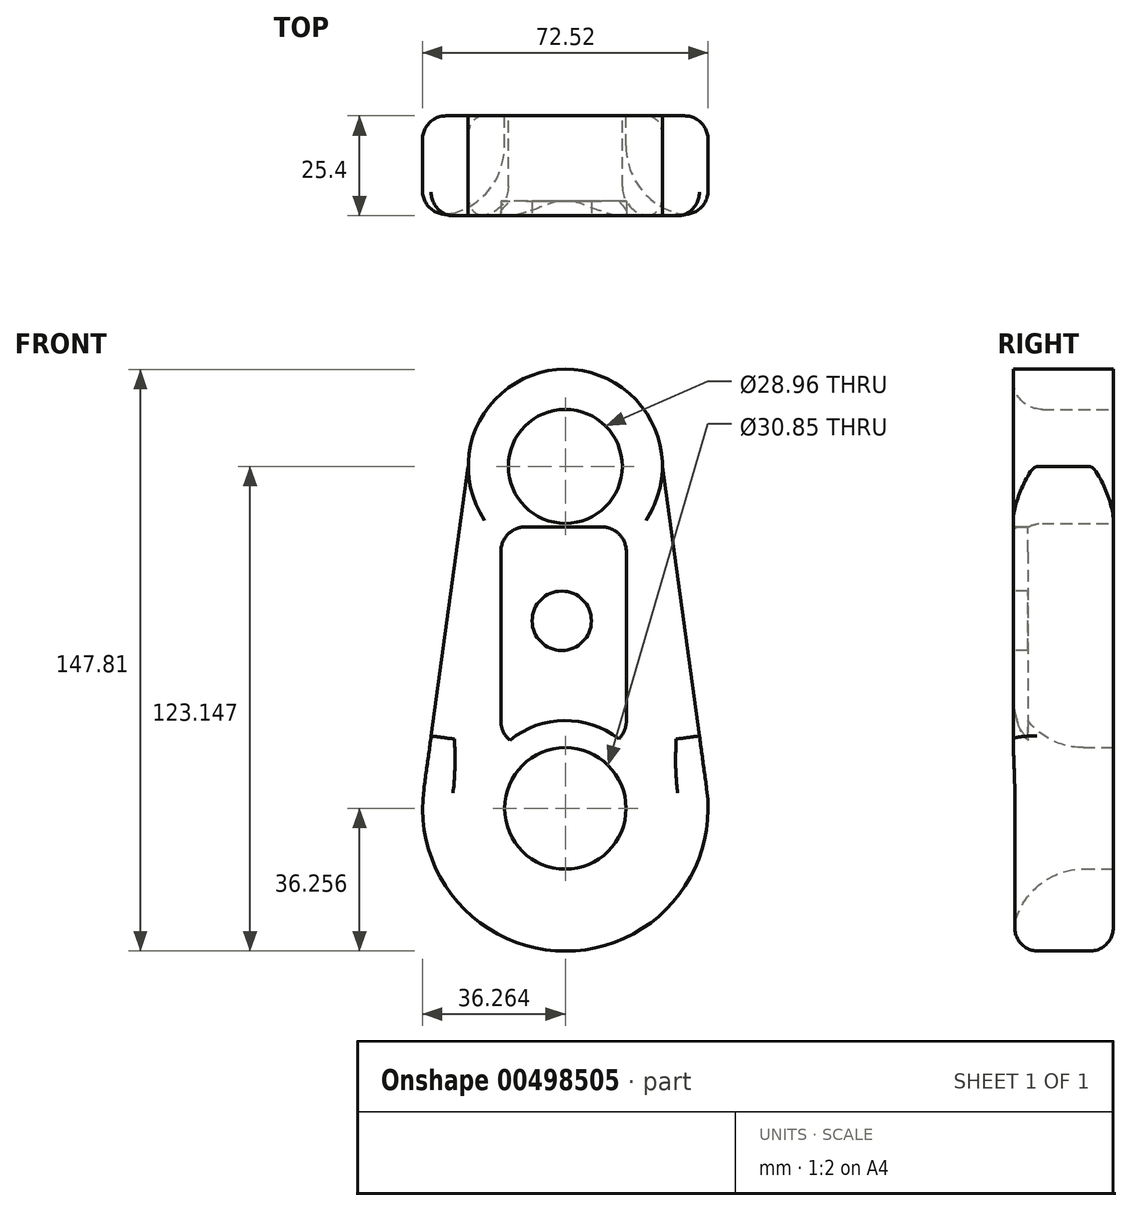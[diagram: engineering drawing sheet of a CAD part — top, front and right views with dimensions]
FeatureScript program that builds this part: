
annotation { "Feature Type Name" : "Feature", "Feature Type Description" : "" }
export const myFeature = defineFeature(function(context is Context, id is Id, definition is map)
    precondition{}
    {
        {
            var Q0;
            Q0=qCreatedBy(makeId("Front.planeOp"),FACE);
            var sketch = newSketch(context, id + "F0", { "sketchPlane" : qUnion([Q0])});
            skCircle(sketch, "E0", {"center": v(-17.79, 39.23) * mm, "radius": 24.67 * mm});
            skCircle(sketch, "E1", {"center": v(-17.79, -47.66) * mm, "radius": 36.26 * mm});
            skLineSegment(sketch, "E2", {"start": v(6.88, 39.23) * mm, "end": v(18.81, -47.66) * mm});
            skLineSegment(sketch, "E3", {"start": v(-42.45, 39.23) * mm, "end": v(-54.39, -47.66) * mm});
            skCircle(sketch, "E4.0", {"center": v(-17.79, 39.23) * mm, "radius": 14.48 * mm});
            skCircle(sketch, "E5.0", {"center": v(-17.79, -47.66) * mm, "radius": 15.43 * mm});
            skSolve(sketch);
        }
        {
            var Q0;
            Q0=makeQuery(id+"F0.imprint","IMPRINT",FACE,{"disambiguationData":[TD([[makeQuery(id+"F0.imprint","IMPRINT",EDGE,{"derivedFrom":sQuery(id+"F0.wireOp",EDGE,"E4.0")}),-1.0]])]});
            var Q1;
            {var subQ0=sQuery(id+"F0.wireOp",EDGE,"E2");var subQ1=sQuery(id+"F0.wireOp",EDGE,"E0");var subQ2=makeQuery(id+"F0.imprint","INTERSECT",VERTEX,{"derivedFrom":[subQ1,subQ0]});Q1=makeQuery(id+"F0.imprint","IMPRINT",FACE,{"disambiguationData":[TD([[makeQuery(id+"F0.imprint","IMPRINT",EDGE,{"disambiguationData":[TD([[subQ2,1.0]])],"derivedFrom":subQ1}),-1.0]])]});}
            var Q2;
            Q2=makeQuery(id+"F0.imprint","IMPRINT",FACE,{"disambiguationData":[TD([[makeQuery(id+"F0.imprint","IMPRINT",EDGE,{"derivedFrom":sQuery(id+"F0.wireOp",EDGE,"E5.0")}),-1.0]])]});
            extrude(context, id + "F1", {"entities" : qUnion([Q0, Q1, Q2]), "depth" : 25.4 * mm});
        }
        {
            var Q0;
            Q0=makeQuery(id+"F1.opExtrude","CAP_FACE",FACE,{"disambiguationData":[OSD([sQuery(id+"F0.wireOp",EDGE,"E0"),sQuery(id+"F0.wireOp",EDGE,"E1"),sQuery(id+"F0.wireOp",EDGE,"E2"),sQuery(id+"F0.wireOp",EDGE,"E3"),sQuery(id+"F0.wireOp",EDGE,"E4.0"),sQuery(id+"F0.wireOp",EDGE,"E5.0")])],"isStart":false});
            var sketch = newSketch(context, id + "F2", { "sketchPlane" : qUnion([Q0])});
            skLineSegment(sketch, "E6.bottom", {"start": v(-27.82, 23.88) * mm, "end": v(-8.62, 23.88) * mm});
            skLineSegment(sketch, "E6.top", {"start": v(-27.82, -31.78) * mm, "end": v(-8.62, -31.78) * mm});
            skLineSegment(sketch, "E6.left", {"start": v(-34.17, 17.53) * mm, "end": v(-34.17, -25.43) * mm});
            skLineSegment(sketch, "E6.right", {"start": v(-2.27, 17.53) * mm, "end": v(-2.27, -25.43) * mm});
            skPoint(sketch, "E7.visualSharp", {"position": v(-2.27, 23.88) * mm});
            skArc(sketch, "E7.filletArc", {"start": v(-2.27, 17.53) * mm, "mid": v(-4.13, 22.02) * mm, "end": v(-8.62, 23.88) * mm});
            skPoint(sketch, "E8.visualSharp", {"position": v(-34.17, 23.88) * mm});
            skArc(sketch, "E8.filletArc", {"start": v(-27.82, 23.88) * mm, "mid": v(-32.3, 22.02) * mm, "end": v(-34.17, 17.53) * mm});
            skPoint(sketch, "E9.visualSharp", {"position": v(-2.27, -31.78) * mm});
            skArc(sketch, "E9.filletArc", {"start": v(-8.62, -31.78) * mm, "mid": v(-4.13, -29.92) * mm, "end": v(-2.27, -25.43) * mm});
            skPoint(sketch, "E10.visualSharp", {"position": v(-34.17, -31.78) * mm});
            skArc(sketch, "E10.filletArc", {"start": v(-34.17, -25.43) * mm, "mid": v(-32.3, -29.92) * mm, "end": v(-27.82, -31.78) * mm});
            skCircle(sketch, "E11", {"center": v(-18.68, 0) * mm, "radius": 7.53 * mm});
            skSolve(sketch);
        }
        {
            var Q0;
            Q0=makeQuery(id+"F2.imprint","IMPRINT",FACE,{"disambiguationData":[TD([[makeQuery(id+"F2.imprint","IMPRINT",EDGE,{"derivedFrom":sQuery(id+"F2.wireOp",EDGE,"E6.bottom")}),-1.0]])]});
            extrude(context, id + "F3", {"entities" : qUnion([Q0]), "operationType" : NewBodyOperationType.REMOVE, "oppositeDirection" : true, "depth" : 3.73 * mm});
        }
        {
            var Q0;
            Q0=makeQuery(id+"F1.opExtrude","CAP_EDGE",EDGE,{"disambiguationData":[OSD([sQuery(id+"F0.wireOp",EDGE,"E5.0")])],"isStart":false});
            fillet(context, id + "F4", {"entities" : qUnion([Q0]), "radius" : 17.77 * mm, "tangentPropagation" : true, "allowEdgeOverflow" : false});
        }
        {
            var Q0;
            Q0=makeQuery(id+"F1.opExtrude","CAP_EDGE",EDGE,{"disambiguationData":[OSD([sQuery(id+"F0.wireOp",EDGE,"E4.0")])],"isStart":false});
            fillet(context, id + "F5", {"entities" : qUnion([Q0]), "radius" : 7.37 * mm, "tangentPropagation" : true, "allowEdgeOverflow" : false});
        }
        {
            var Q0;
            Q0=makeQuery(id+"F1.opExtrude","CAP_EDGE",EDGE,{"disambiguationData":[OSD([sQuery(id+"F0.wireOp",EDGE,"E3")])],"isStart":true});
            var Q1;
            Q1=makeQuery(id+"F1.opExtrude","CAP_EDGE",EDGE,{"disambiguationData":[OSD([sQuery(id+"F0.wireOp",EDGE,"E3")])],"isStart":false});
            var Q2;
            Q2=makeQuery(id+"F1.opExtrude","CAP_EDGE",EDGE,{"disambiguationData":[OSD([sQuery(id+"F0.wireOp",EDGE,"E2")])],"isStart":false});
            var Q3;
            Q3=makeQuery(id+"F1.opExtrude","CAP_EDGE",EDGE,{"disambiguationData":[OSD([sQuery(id+"F0.wireOp",EDGE,"E2")])],"isStart":true});
            fillet(context, id + "F6", {"entities" : qUnion([Q0, Q1, Q2, Q3]), "radius" : 5.97 * mm, "tangentPropagation" : true, "allowEdgeOverflow" : false});
        }
    });
